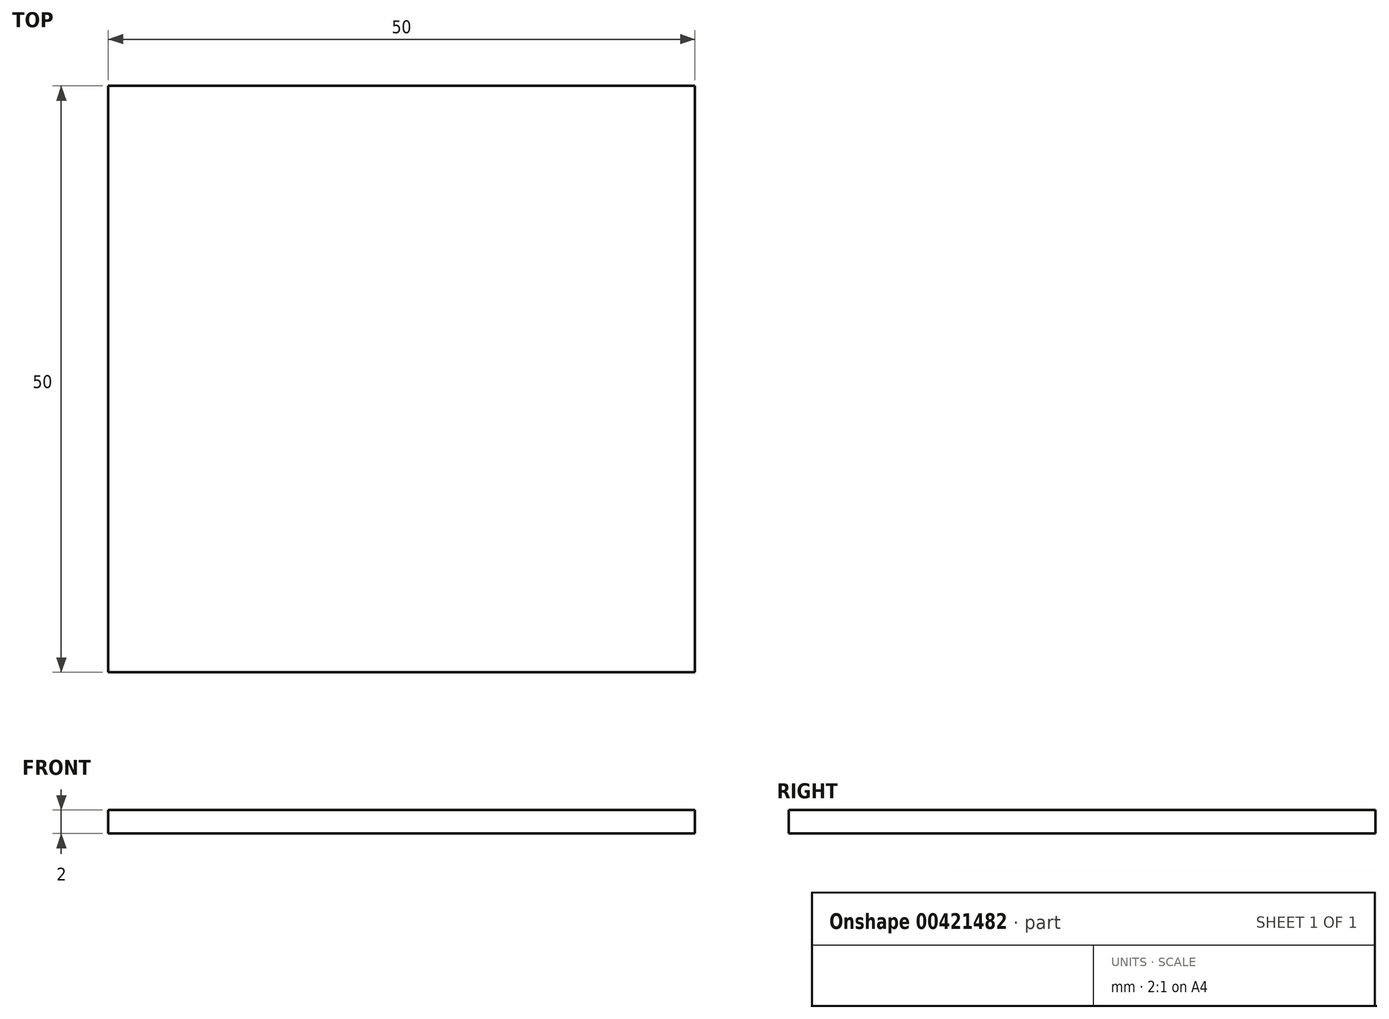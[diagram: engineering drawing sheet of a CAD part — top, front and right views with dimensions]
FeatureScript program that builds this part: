
annotation { "Feature Type Name" : "Feature", "Feature Type Description" : "" }
export const myFeature = defineFeature(function(context is Context, id is Id, definition is map)
    precondition{}
    {
        {
            var Q0;
            Q0=qCreatedBy(makeId("Top.planeOp"),FACE);
            var sketch = newSketch(context, id + "F0", { "sketchPlane" : qUnion([Q0])});
            skLineSegment(sketch, "E0.bottom", {"start": v(0, 0) * mm, "end": v(-50, 0) * mm});
            skLineSegment(sketch, "E0.top", {"start": v(0, -50) * mm, "end": v(-50, -50) * mm});
            skLineSegment(sketch, "E0.left", {"start": v(0, 0) * mm, "end": v(0, -50) * mm});
            skLineSegment(sketch, "E0.right", {"start": v(-50, 0) * mm, "end": v(-50, -50) * mm});
            skSolve(sketch);
        }
        {
            var Q0;
            Q0 = qSketchRegion(id + "F0", true);
            extrude(context, id + "F1", {"entities" : qUnion([Q0]), "depth" : 2 * mm});
        }
    });
